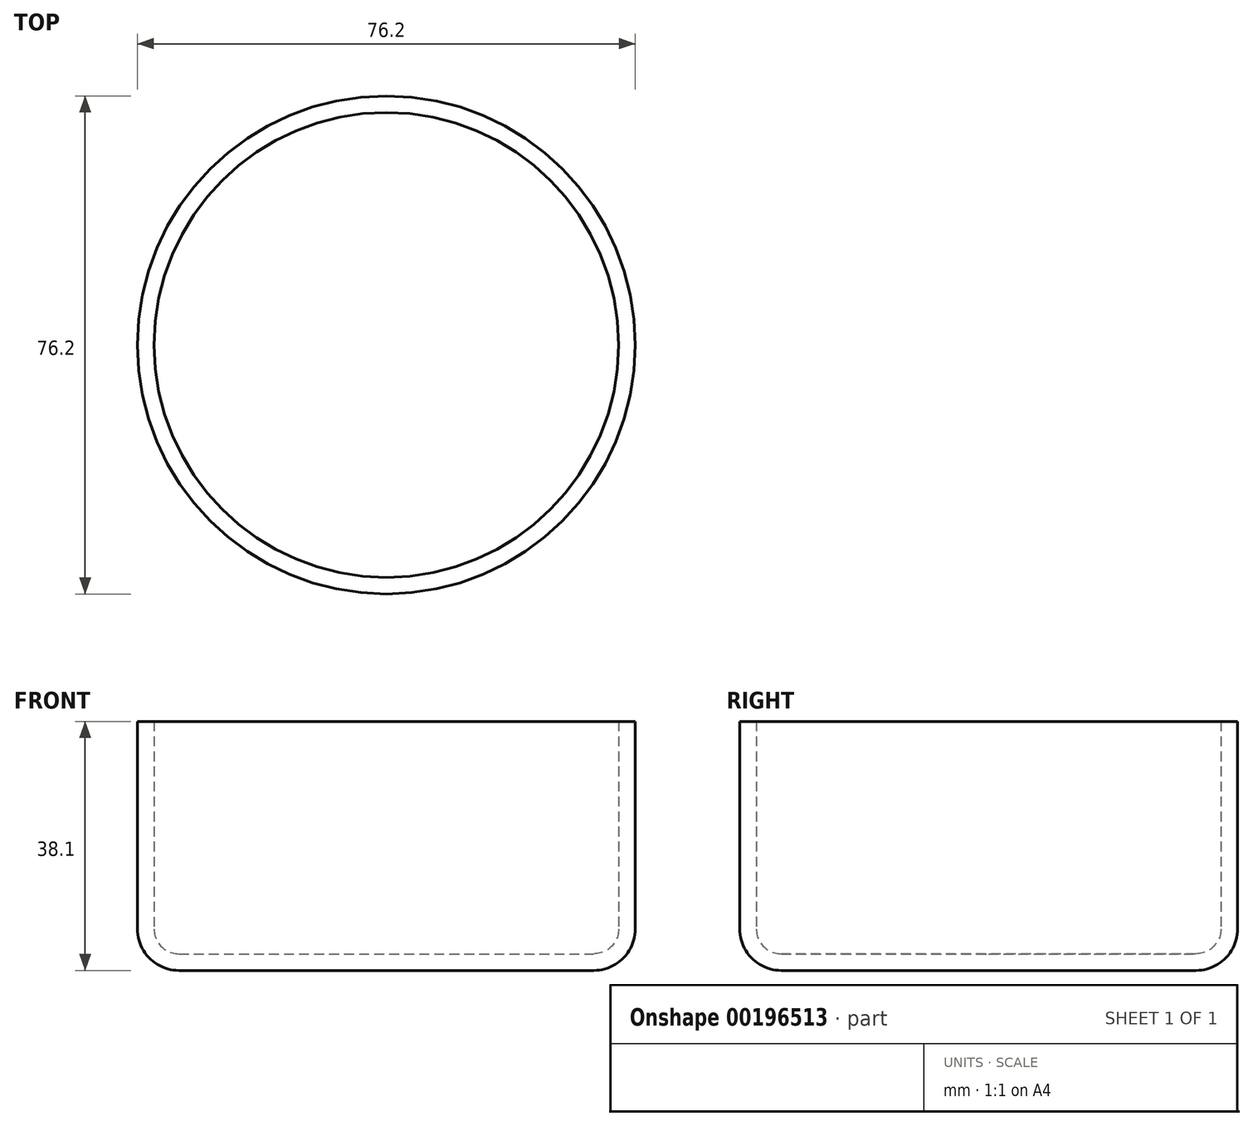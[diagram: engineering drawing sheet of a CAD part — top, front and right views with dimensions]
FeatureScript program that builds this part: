
annotation { "Feature Type Name" : "Feature", "Feature Type Description" : "" }
export const myFeature = defineFeature(function(context is Context, id is Id, definition is map)
    precondition{}
    {
        {
            var Q0;
            Q0=qCreatedBy(makeId("Front.planeOp"),FACE);
            var sketch = newSketch(context, id + "F0", { "sketchPlane" : qUnion([Q0])});
            skLineSegment(sketch, "E0.bottom", {"start": v(0, 0) * mm, "end": v(31.75, 0) * mm});
            skLineSegment(sketch, "E0.top", {"start": v(0, 38.1) * mm, "end": v(38.1, 38.1) * mm});
            skLineSegment(sketch, "E0.left", {"start": v(0, 0) * mm, "end": v(0, 38.1) * mm});
            skLineSegment(sketch, "E0.right", {"start": v(38.1, 6.35) * mm, "end": v(38.1, 38.1) * mm});
            skPoint(sketch, "E1.visualSharp", {"position": v(38.1, 0) * mm});
            skArc(sketch, "E1.filletArc", {"start": v(31.75, 0) * mm, "mid": v(36.24, 1.86) * mm, "end": v(38.1, 6.35) * mm});
            skLineSegment(sketch, "E2", {"start": v(0, 0) * mm, "end": v(0, 44.37) * mm, "construction": true});
            skSolve(sketch);
        }
        {
            var Q0;
            Q0=makeQuery(id+"F0.imprint","IMPRINT",FACE,{"disambiguationData":[TD([[makeQuery(id+"F0.imprint","IMPRINT",EDGE,{"derivedFrom":sQuery(id+"F0.wireOp",EDGE,"E0.bottom")}),1.0]])]});
            var Q1;
            Q1=sQuery(id+"F0.wireOp",EDGE,"E2");
            revolve(context, id + "F1", {"entities" : qUnion([Q0]), "axis" : qUnion([Q1]), "revolveType" : RevolveType.FULL});
        }
        {
            var Q0;
            Q0=makeQuery(id+"F1.opRevolve","SWEPT_FACE",FACE,{"disambiguationData":[OSD([sQuery(id+"F0.wireOp",EDGE,"E0.top")])]});
            shell(context, id + "F2", {"entities" : qUnion([Q0]), "thickness" : 2.54 * mm});
        }
    });
